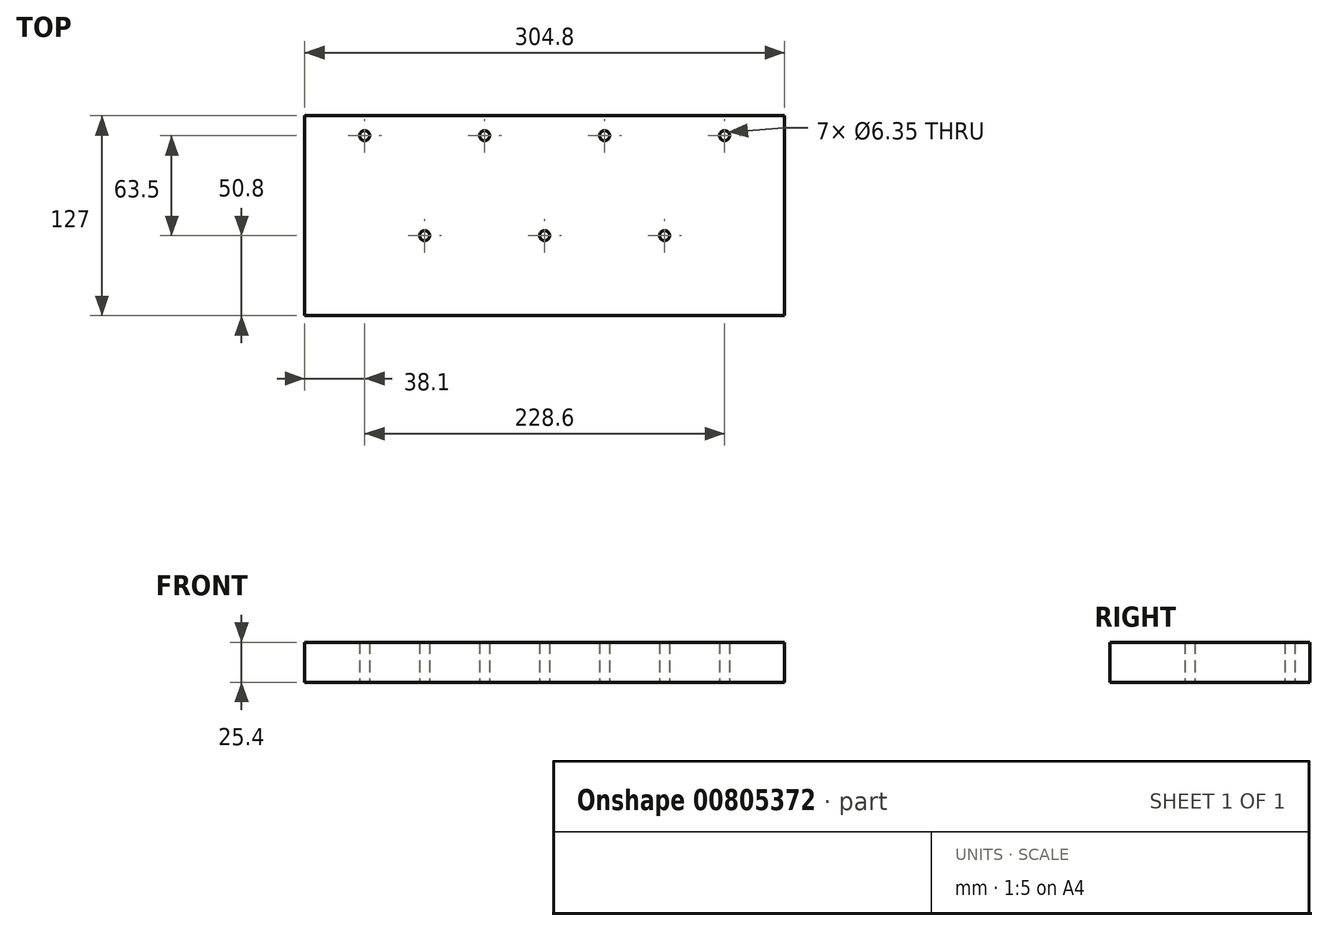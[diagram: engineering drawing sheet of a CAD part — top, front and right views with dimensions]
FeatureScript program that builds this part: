
annotation { "Feature Type Name" : "Feature", "Feature Type Description" : "" }
export const myFeature = defineFeature(function(context is Context, id is Id, definition is map)
    precondition{}
    {
        {
            var Q0;
            Q0=qCreatedBy(makeId("Top.planeOp"),FACE);
            var sketch = newSketch(context, id + "F0", { "sketchPlane" : qUnion([Q0])});
            skLineSegment(sketch, "E0.bottom", {"start": v(0, 0) * mm, "end": v(304.8, 0) * mm});
            skLineSegment(sketch, "E0.top", {"start": v(0, 127) * mm, "end": v(304.8, 127) * mm});
            skLineSegment(sketch, "E0.left", {"start": v(0, 0) * mm, "end": v(0, 127) * mm});
            skLineSegment(sketch, "E0.right", {"start": v(304.8, 0) * mm, "end": v(304.8, 127) * mm});
            skCircle(sketch, "E1", {"center": v(38.1, 114.3) * mm, "radius": 3.18 * mm});
            skCircle(sketch, "E2.1.0.0", {"center": v(114.3, 114.3) * mm, "radius": 3.18 * mm});
            skCircle(sketch, "E2.2.0.0", {"center": v(190.5, 114.3) * mm, "radius": 3.18 * mm});
            skCircle(sketch, "E2.3.0.0", {"center": v(266.7, 114.3) * mm, "radius": 3.18 * mm});
            skLineSegment(sketch, "E2.direction1", {"start": v(38.1, 114.3) * mm, "end": v(114.3, 114.3) * mm, "construction": true});
            skCircle(sketch, "E3", {"center": v(76.2, 50.8) * mm, "radius": 3.17 * mm});
            skPoint(sketch, "E3.centerSnap0", {"position": v(76.2, 114.3) * mm});
            skCircle(sketch, "E4.1.0.0", {"center": v(152.4, 50.8) * mm, "radius": 3.17 * mm});
            skCircle(sketch, "E4.2.0.0", {"center": v(228.6, 50.8) * mm, "radius": 3.17 * mm});
            skLineSegment(sketch, "E4.direction1", {"start": v(76.2, 50.8) * mm, "end": v(152.4, 50.8) * mm, "construction": true});
            skSolve(sketch);
        }
        {
            var Q0;
            Q0 = qSketchRegion(id + "F0", true);
            extrude(context, id + "F1", {"entities" : qUnion([Q0]), "depth" : 25.4 * mm, "offsetDistance" : 25.4 * mm});
        }
    });
